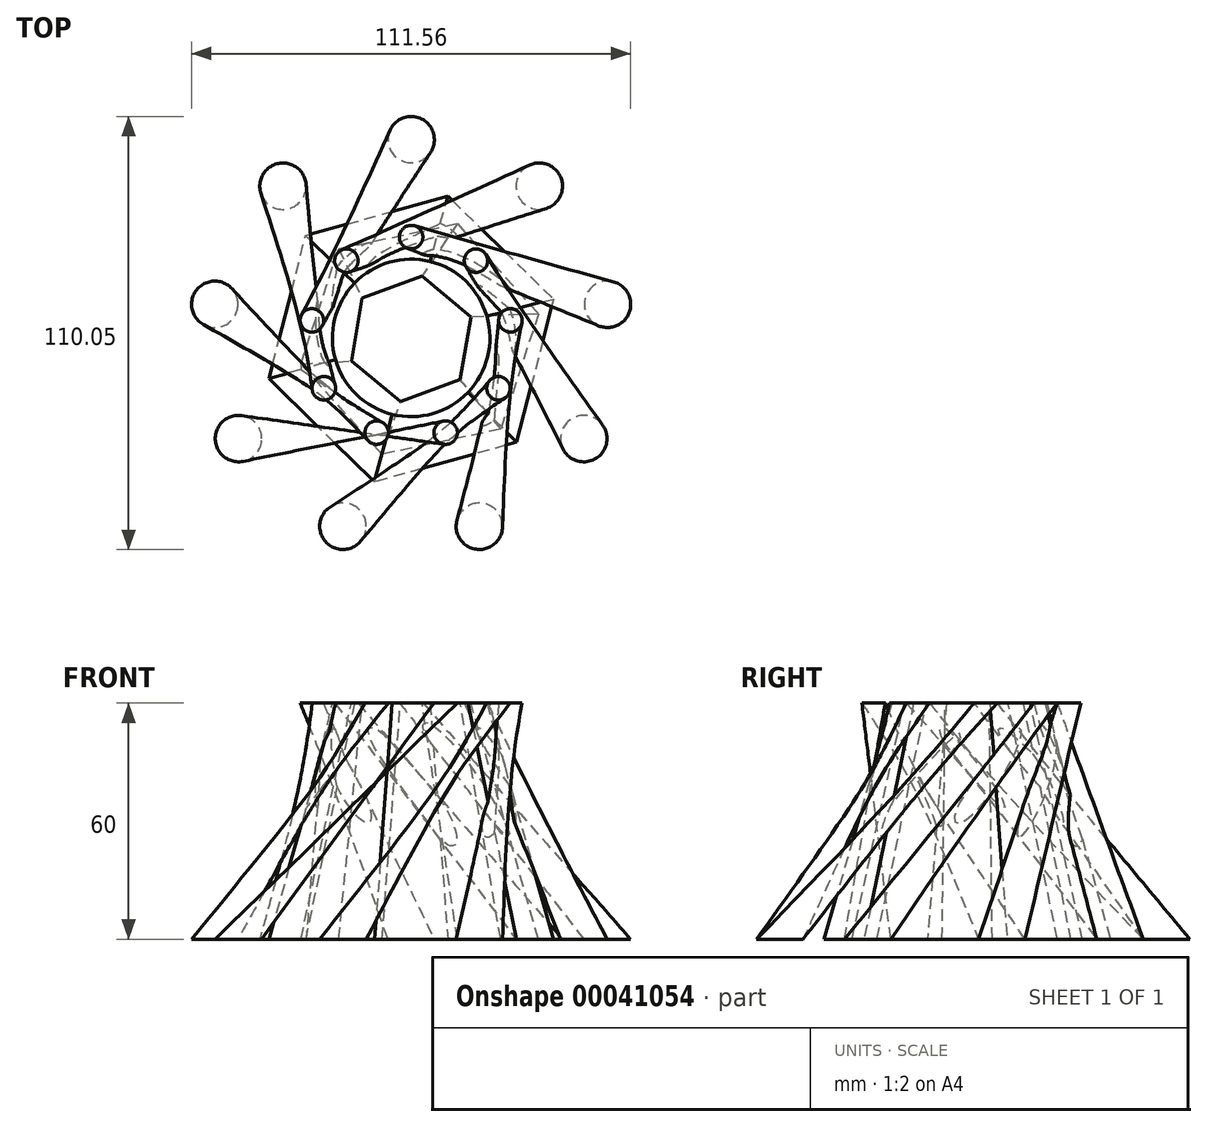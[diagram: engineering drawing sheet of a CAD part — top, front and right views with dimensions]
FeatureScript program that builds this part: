
annotation { "Feature Type Name" : "Feature", "Feature Type Description" : "" }
export const myFeature = defineFeature(function(context is Context, id is Id, definition is map)
    precondition{}
    {
        {
            var Q0;
            Q0=qCreatedBy(makeId("Top.planeOp"),FACE);
            var sketch = newSketch(context, id + "F0", { "sketchPlane" : qUnion([Q0])});
            skCircle(sketch, "E0", {"center": v(0, 50.65) * mm, "radius": 5.9 * mm});
            skCircle(sketch, "E1.1.0", {"center": v(-32.56, 38.8) * mm, "radius": 5.9 * mm});
            skCircle(sketch, "E1.2.0", {"center": v(-49.88, 8.8) * mm, "radius": 5.9 * mm});
            skCircle(sketch, "E1.3.0", {"center": v(-43.87, -25.33) * mm, "radius": 5.9 * mm});
            skCircle(sketch, "E1.4.0", {"center": v(-17.32, -47.6) * mm, "radius": 5.9 * mm});
            skCircle(sketch, "E1.5.0", {"center": v(17.32, -47.6) * mm, "radius": 5.9 * mm});
            skCircle(sketch, "E1.6.0", {"center": v(43.87, -25.33) * mm, "radius": 5.9 * mm});
            skCircle(sketch, "E1.7.0", {"center": v(49.88, 8.8) * mm, "radius": 5.9 * mm});
            skCircle(sketch, "E1.8.0", {"center": v(32.56, 38.8) * mm, "radius": 5.9 * mm});
            skPoint(sketch, "E1.center", {"position": v(0, 0) * mm});
            skCircle(sketch, "E2.cCircle", {"center": v(0, 0) * mm, "radius": 32.5 * mm, "construction": true});
            skLineSegment(sketch, "E2.0", {"start": v(-36.13, -10.12) * mm, "end": v(-26.83, 26.23) * mm});
            skLineSegment(sketch, "E2.1", {"start": v(-26.83, 26.23) * mm, "end": v(9.3, 36.35) * mm});
            skLineSegment(sketch, "E2.2", {"start": v(9.3, 36.35) * mm, "end": v(36.13, 10.12) * mm});
            skLineSegment(sketch, "E2.3", {"start": v(36.13, 10.12) * mm, "end": v(26.83, -26.23) * mm});
            skLineSegment(sketch, "E2.4", {"start": v(26.83, -26.23) * mm, "end": v(-9.3, -36.35) * mm});
            skLineSegment(sketch, "E2.5", {"start": v(-9.3, -36.35) * mm, "end": v(-36.13, -10.12) * mm});
            skPoint(sketch, "E2.0.midPoint", {"position": v(-31.48, 8.06) * mm});
            skSolve(sketch);
        }
        {
            var Q0;
            Q0=qCreatedBy(makeId("Top.planeOp"),FACE);
            cPlane(context, id + "F1", {"entities" : qUnion([Q0]), "cplaneType" : CPlaneType.OFFSET, "offset" : 60 * mm, "width" : 150 * mm, "height" : 150 * mm});
        }
        {
            var Q0;
            Q0=qCreatedBy(id+"F1.planeOp",FACE);
            var sketch = newSketch(context, id + "F2", { "sketchPlane" : qUnion([Q0])});
            skCircle(sketch, "E3", {"center": v(0, 0.27) * mm, "radius": 20 * mm});
            skCircle(sketch, "E4", {"center": v(0, 25.88) * mm, "radius": 2.98 * mm});
            skCircle(sketch, "E5.1.0", {"center": v(-16.46, 19.89) * mm, "radius": 2.98 * mm});
            skCircle(sketch, "E5.2.0", {"center": v(-25.22, 4.71) * mm, "radius": 2.98 * mm});
            skCircle(sketch, "E5.3.0", {"center": v(-22.18, -12.54) * mm, "radius": 2.98 * mm});
            skCircle(sketch, "E5.4.0", {"center": v(-8.76, -23.8) * mm, "radius": 2.98 * mm});
            skCircle(sketch, "E5.5.0", {"center": v(8.76, -23.8) * mm, "radius": 2.98 * mm});
            skCircle(sketch, "E5.6.0", {"center": v(22.18, -12.54) * mm, "radius": 2.98 * mm});
            skCircle(sketch, "E5.7.0", {"center": v(25.22, 4.71) * mm, "radius": 2.98 * mm});
            skCircle(sketch, "E5.8.0", {"center": v(16.46, 19.89) * mm, "radius": 2.98 * mm});
            skSolve(sketch);
        }
        {
            var Q0;
            Q0=makeQuery(id+"F2.imprint","IMPRINT",FACE,{"disambiguationData":[TD([[makeQuery(id+"F2.imprint","IMPRINT",EDGE,{"derivedFrom":sQuery(id+"F2.wireOp",EDGE,"E3")}),1.0]])]});
            var Q1;
            Q1=makeQuery(id+"F0.imprint","IMPRINT",FACE,{"disambiguationData":[TD([[makeQuery(id+"F0.imprint","IMPRINT",EDGE,{"derivedFrom":sQuery(id+"F0.wireOp",EDGE,"E2.0")}),-1.0]])]});
            loft(context, id + "F3", {"sheetProfilesArray" : [{ "sheetProfileEntities" : qUnion([Q0]) }, { "sheetProfileEntities" : qUnion([Q1]) }]});
        }
        {
            var Q0;
            Q0=makeQuery(id+"F0.imprint","IMPRINT",FACE,{"disambiguationData":[TD([[makeQuery(id+"F0.imprint","IMPRINT",EDGE,{"derivedFrom":sQuery(id+"F0.wireOp",EDGE,"E1.4.0")}),1.0]])]});
            var Q1;
            Q1=makeQuery(id+"F2.imprint","IMPRINT",FACE,{"disambiguationData":[TD([[makeQuery(id+"F2.imprint","IMPRINT",EDGE,{"derivedFrom":sQuery(id+"F2.wireOp",EDGE,"E5.6.0")}),1.0]])]});
            loft(context, id + "F4", {"sheetProfilesArray" : [{ "sheetProfileEntities" : qUnion([Q0]) }, { "sheetProfileEntities" : qUnion([Q1]) }]});
        }
        {
            var Q1;
            Q1=makeQuery(id+"F0.imprint","IMPRINT",FACE,{"disambiguationData":[TD([[makeQuery(id+"F0.imprint","IMPRINT",EDGE,{"derivedFrom":sQuery(id+"F0.wireOp",EDGE,"E1.5.0")}),1.0]])]});
            var Q2;
            Q2=makeQuery(id+"F2.imprint","IMPRINT",FACE,{"disambiguationData":[TD([[makeQuery(id+"F2.imprint","IMPRINT",EDGE,{"derivedFrom":sQuery(id+"F2.wireOp",EDGE,"E5.7.0")}),1.0]])]});
            loft(context, id + "F5", {"operationType" : NewBodyOperationType.ADD, "sheetProfilesArray" : [{ "sheetProfileEntities" : qUnion([Q1]) }, { "sheetProfileEntities" : qUnion([Q2]) }]});
        }
        {
            var Q1;
            Q1=makeQuery(id+"F0.imprint","IMPRINT",FACE,{"disambiguationData":[TD([[makeQuery(id+"F0.imprint","IMPRINT",EDGE,{"derivedFrom":sQuery(id+"F0.wireOp",EDGE,"E1.6.0")}),1.0]])]});
            var Q2;
            Q2=makeQuery(id+"F2.imprint","IMPRINT",FACE,{"disambiguationData":[TD([[makeQuery(id+"F2.imprint","IMPRINT",EDGE,{"derivedFrom":sQuery(id+"F2.wireOp",EDGE,"E5.8.0")}),1.0]])]});
            loft(context, id + "F6", {"operationType" : NewBodyOperationType.ADD, "sheetProfilesArray" : [{ "sheetProfileEntities" : qUnion([Q1]) }, { "sheetProfileEntities" : qUnion([Q2]) }]});
        }
        {
            var Q1;
            Q1=makeQuery(id+"F0.imprint","IMPRINT",FACE,{"disambiguationData":[TD([[makeQuery(id+"F0.imprint","IMPRINT",EDGE,{"derivedFrom":sQuery(id+"F0.wireOp",EDGE,"E1.3.0")}),1.0]])]});
            var Q2;
            Q2=makeQuery(id+"F2.imprint","IMPRINT",FACE,{"disambiguationData":[TD([[makeQuery(id+"F2.imprint","IMPRINT",EDGE,{"derivedFrom":sQuery(id+"F2.wireOp",EDGE,"E5.5.0")}),1.0]])]});
            loft(context, id + "F7", {"operationType" : NewBodyOperationType.ADD, "sheetProfilesArray" : [{ "sheetProfileEntities" : qUnion([Q1]) }, { "sheetProfileEntities" : qUnion([Q2]) }]});
        }
        {
            var Q1;
            Q1=makeQuery(id+"F0.imprint","IMPRINT",FACE,{"disambiguationData":[TD([[makeQuery(id+"F0.imprint","IMPRINT",EDGE,{"derivedFrom":sQuery(id+"F0.wireOp",EDGE,"E1.2.0")}),1.0]])]});
            var Q2;
            Q2=makeQuery(id+"F2.imprint","IMPRINT",FACE,{"disambiguationData":[TD([[makeQuery(id+"F2.imprint","IMPRINT",EDGE,{"derivedFrom":sQuery(id+"F2.wireOp",EDGE,"E5.4.0")}),1.0]])]});
            loft(context, id + "F8", {"operationType" : NewBodyOperationType.ADD, "sheetProfilesArray" : [{ "sheetProfileEntities" : qUnion([Q1]) }, { "sheetProfileEntities" : qUnion([Q2]) }]});
        }
        {
            var Q1;
            Q1=makeQuery(id+"F0.imprint","IMPRINT",FACE,{"disambiguationData":[TD([[makeQuery(id+"F0.imprint","IMPRINT",EDGE,{"derivedFrom":sQuery(id+"F0.wireOp",EDGE,"E1.1.0")}),1.0]])]});
            var Q2;
            Q2=makeQuery(id+"F2.imprint","IMPRINT",FACE,{"disambiguationData":[TD([[makeQuery(id+"F2.imprint","IMPRINT",EDGE,{"derivedFrom":sQuery(id+"F2.wireOp",EDGE,"E5.3.0")}),1.0]])]});
            loft(context, id + "F9", {"operationType" : NewBodyOperationType.ADD, "sheetProfilesArray" : [{ "sheetProfileEntities" : qUnion([Q1]) }, { "sheetProfileEntities" : qUnion([Q2]) }]});
        }
        {
            var Q1;
            Q1=makeQuery(id+"F0.imprint","IMPRINT",FACE,{"disambiguationData":[TD([[makeQuery(id+"F0.imprint","IMPRINT",EDGE,{"derivedFrom":sQuery(id+"F0.wireOp",EDGE,"E0")}),1.0]])]});
            var Q2;
            Q2=makeQuery(id+"F2.imprint","IMPRINT",FACE,{"disambiguationData":[TD([[makeQuery(id+"F2.imprint","IMPRINT",EDGE,{"derivedFrom":sQuery(id+"F2.wireOp",EDGE,"E5.2.0")}),1.0]])]});
            loft(context, id + "F10", {"operationType" : NewBodyOperationType.ADD, "sheetProfilesArray" : [{ "sheetProfileEntities" : qUnion([Q1]) }, { "sheetProfileEntities" : qUnion([Q2]) }]});
        }
        {
            var Q1;
            Q1=makeQuery(id+"F0.imprint","IMPRINT",FACE,{"disambiguationData":[TD([[makeQuery(id+"F0.imprint","IMPRINT",EDGE,{"derivedFrom":sQuery(id+"F0.wireOp",EDGE,"E1.7.0")}),1.0]])]});
            var Q2;
            Q2=makeQuery(id+"F2.imprint","IMPRINT",FACE,{"disambiguationData":[TD([[makeQuery(id+"F2.imprint","IMPRINT",EDGE,{"derivedFrom":sQuery(id+"F2.wireOp",EDGE,"E4")}),1.0]])]});
            loft(context, id + "F11", {"operationType" : NewBodyOperationType.ADD, "sheetProfilesArray" : [{ "sheetProfileEntities" : qUnion([Q1]) }, { "sheetProfileEntities" : qUnion([Q2]) }]});
        }
        {
            var Q1;
            Q1=makeQuery(id+"F0.imprint","IMPRINT",FACE,{"disambiguationData":[TD([[makeQuery(id+"F0.imprint","IMPRINT",EDGE,{"derivedFrom":sQuery(id+"F0.wireOp",EDGE,"E1.8.0")}),1.0]])]});
            var Q2;
            Q2=makeQuery(id+"F2.imprint","IMPRINT",FACE,{"disambiguationData":[TD([[makeQuery(id+"F2.imprint","IMPRINT",EDGE,{"derivedFrom":sQuery(id+"F2.wireOp",EDGE,"E5.1.0")}),1.0]])]});
            loft(context, id + "F12", {"operationType" : NewBodyOperationType.ADD, "sheetProfilesArray" : [{ "sheetProfileEntities" : qUnion([Q1]) }, { "sheetProfileEntities" : qUnion([Q2]) }]});
        }
        {
            var Q0;
            Q0=makeQuery(id+"F2.imprint","IMPRINT",FACE,{"disambiguationData":[TD([[makeQuery(id+"F2.imprint","IMPRINT",EDGE,{"derivedFrom":sQuery(id+"F2.wireOp",EDGE,"E3")}),1.0]])]});
            var sketch = newSketch(context, id + "F13", { "sketchPlane" : qUnion([Q0])});
            skCircle(sketch, "E6.cCircle", {"center": v(0, 0) * mm, "radius": 14.02 * mm, "construction": true});
            skLineSegment(sketch, "E6.0", {"start": v(-2.75, -15.95) * mm, "end": v(-15.19, -5.6) * mm});
            skLineSegment(sketch, "E6.1", {"start": v(-15.19, -5.6) * mm, "end": v(-12.44, 10.35) * mm});
            skLineSegment(sketch, "E6.2", {"start": v(-12.44, 10.35) * mm, "end": v(2.75, 15.95) * mm});
            skLineSegment(sketch, "E6.3", {"start": v(2.75, 15.95) * mm, "end": v(15.19, 5.6) * mm});
            skLineSegment(sketch, "E6.4", {"start": v(15.19, 5.6) * mm, "end": v(12.44, -10.35) * mm});
            skLineSegment(sketch, "E6.5", {"start": v(12.44, -10.35) * mm, "end": v(-2.75, -15.95) * mm});
            skPoint(sketch, "E6.0.midPoint", {"position": v(-8.97, -10.77) * mm});
            skSolve(sketch);
        }
        {
            var Q0;
            Q0=makeQuery(id+"F0.imprint","IMPRINT",FACE,{"disambiguationData":[TD([[makeQuery(id+"F0.imprint","IMPRINT",EDGE,{"derivedFrom":sQuery(id+"F0.wireOp",EDGE,"E2.0")}),-1.0]])]});
            var sketch = newSketch(context, id + "F14", { "sketchPlane" : qUnion([Q0])});
            skCircle(sketch, "E7.cCircle", {"center": v(2.18, 0) * mm, "radius": 26.7 * mm, "construction": true});
            skLineSegment(sketch, "E7.0", {"start": v(22.77, -22.93) * mm, "end": v(-7.39, -29.3) * mm});
            skLineSegment(sketch, "E7.1", {"start": v(-7.39, -29.3) * mm, "end": v(-27.98, -6.37) * mm});
            skLineSegment(sketch, "E7.2", {"start": v(-27.98, -6.37) * mm, "end": v(-18.42, 22.93) * mm});
            skLineSegment(sketch, "E7.3", {"start": v(-18.42, 22.93) * mm, "end": v(11.74, 29.3) * mm});
            skLineSegment(sketch, "E7.4", {"start": v(11.74, 29.3) * mm, "end": v(32.33, 6.37) * mm});
            skLineSegment(sketch, "E7.5", {"start": v(32.33, 6.37) * mm, "end": v(22.77, -22.93) * mm});
            skPoint(sketch, "E7.0.midPoint", {"position": v(7.7, -26.12) * mm});
            skSolve(sketch);
        }
        {
            var Q1;
            Q1=makeQuery(id+"F14.imprint","IMPRINT",FACE,{"disambiguationData":[TD([[makeQuery(id+"F14.imprint","IMPRINT",EDGE,{"derivedFrom":sQuery(id+"F14.wireOp",EDGE,"E7.0")}),-1.0]])]});
            var Q2;
            Q2=makeQuery(id+"F13.imprint","IMPRINT",FACE,{"disambiguationData":[TD([[makeQuery(id+"F13.imprint","IMPRINT",EDGE,{"derivedFrom":sQuery(id+"F13.wireOp",EDGE,"E6.0")}),-1.0]])]});
            loft(context, id + "F15", {"operationType" : NewBodyOperationType.REMOVE, "sheetProfilesArray" : [{ "sheetProfileEntities" : qUnion([Q1]) }, { "sheetProfileEntities" : qUnion([Q2]) }]});
        }
    });
